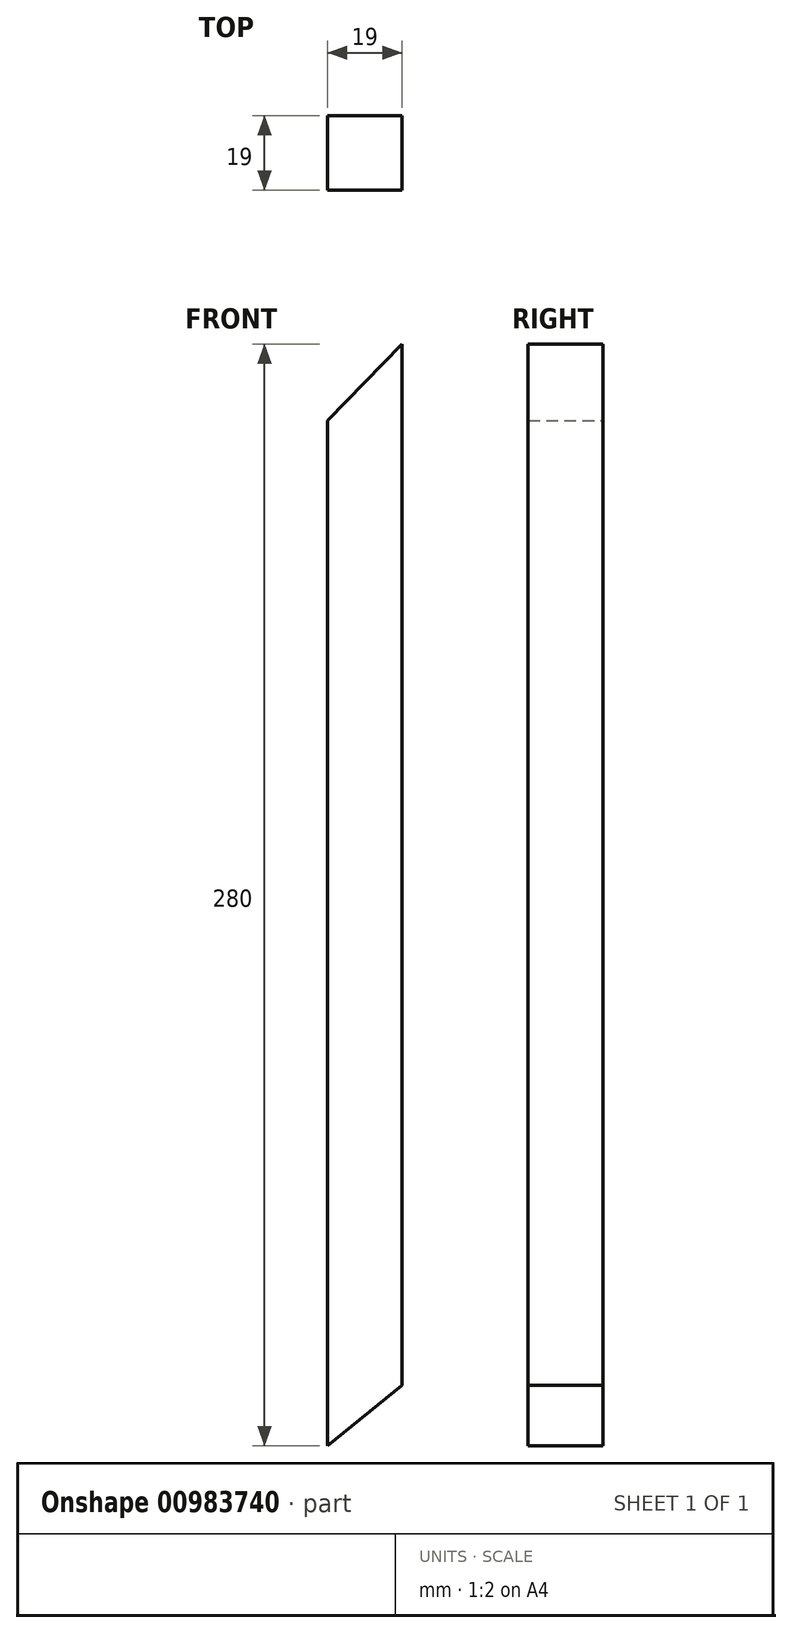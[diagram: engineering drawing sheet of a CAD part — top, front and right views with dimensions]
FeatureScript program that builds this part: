
annotation { "Feature Type Name" : "Feature", "Feature Type Description" : "" }
export const myFeature = defineFeature(function(context is Context, id is Id, definition is map)
    precondition{}
    {
        {
            var Q0;
            Q0=qCreatedBy(makeId("Front.planeOp"),FACE);
            var sketch = newSketch(context, id + "F0", { "sketchPlane" : qUnion([Q0])});
            skLineSegment(sketch, "E0.bottom", {"start": v(8.64, -25.24) * mm, "end": v(-10.36, -25.24) * mm});
            skLineSegment(sketch, "E0.left", {"start": v(8.64, -9.78) * mm, "end": v(8.64, 254.76) * mm});
            skLineSegment(sketch, "E0.right", {"start": v(-10.36, -25.24) * mm, "end": v(-10.36, 235.22) * mm});
            skLineSegment(sketch, "E1", {"start": v(8.64, 254.76) * mm, "end": v(-10.36, 235.22) * mm});
            skLineSegment(sketch, "E2", {"start": v(-10.36, -25.24) * mm, "end": v(8.64, -9.78) * mm});
            skSolve(sketch);
        }
        {
            var Q0;
            Q0 = qSketchRegion(id + "F0", true);
            extrude(context, id + "F1", {"entities" : qUnion([Q0]), "depth" : 19 * mm, "offsetDistance" : 25.4 * mm});
        }
    });
